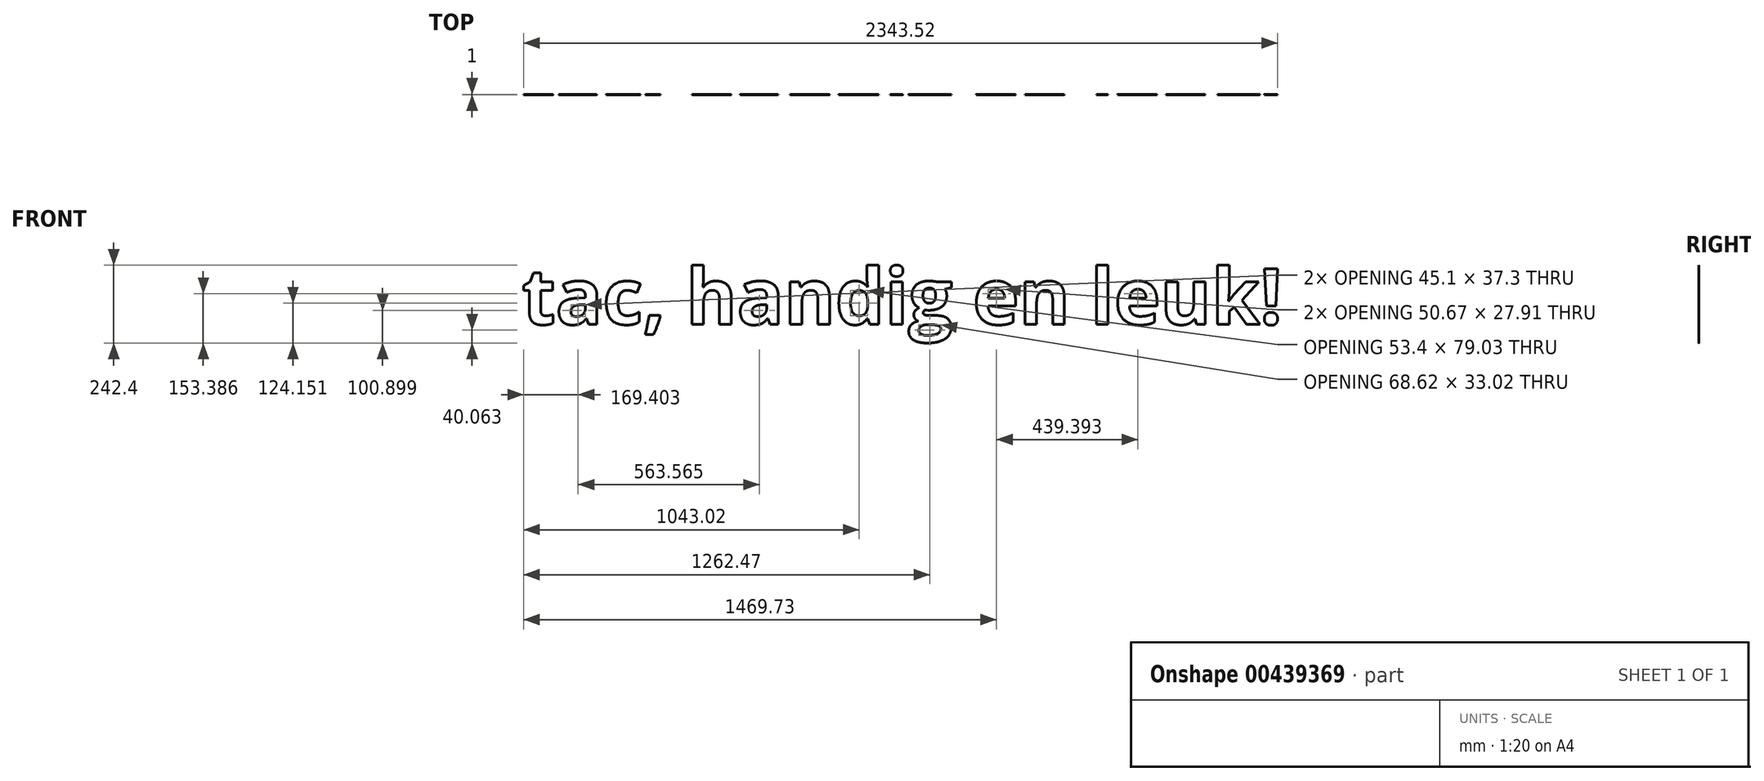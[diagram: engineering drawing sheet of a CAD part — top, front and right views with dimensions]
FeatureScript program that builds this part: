
annotation { "Feature Type Name" : "Feature", "Feature Type Description" : "" }
export const myFeature = defineFeature(function(context is Context, id is Id, definition is map)
    precondition{}
    {
        {
            var Q0;
            Q0=qCreatedBy(makeId("Front.planeOp"),FACE);
            var sketch = newSketch(context, id + "F0", { "sketchPlane" : qUnion([Q0])});
            skText(sketch, "E0", { "text": "tac, handig en leuk!", "fontName": "OpenSans-Bold.ttf"});
            const initialGuessF0  = {"E0": [-1.2, -0.08303, 1, 0, 0.1745]};
            skSetInitialGuess(sketch, initialGuessF0);
            skSolve(sketch);
        }
        {
            var Q0;
            Q0 = qSketchRegion(id + "F0", true);
            extrude(context, id + "F1", {"entities" : qUnion([Q0]), "depth" : 1 * mm});
        }
    });
